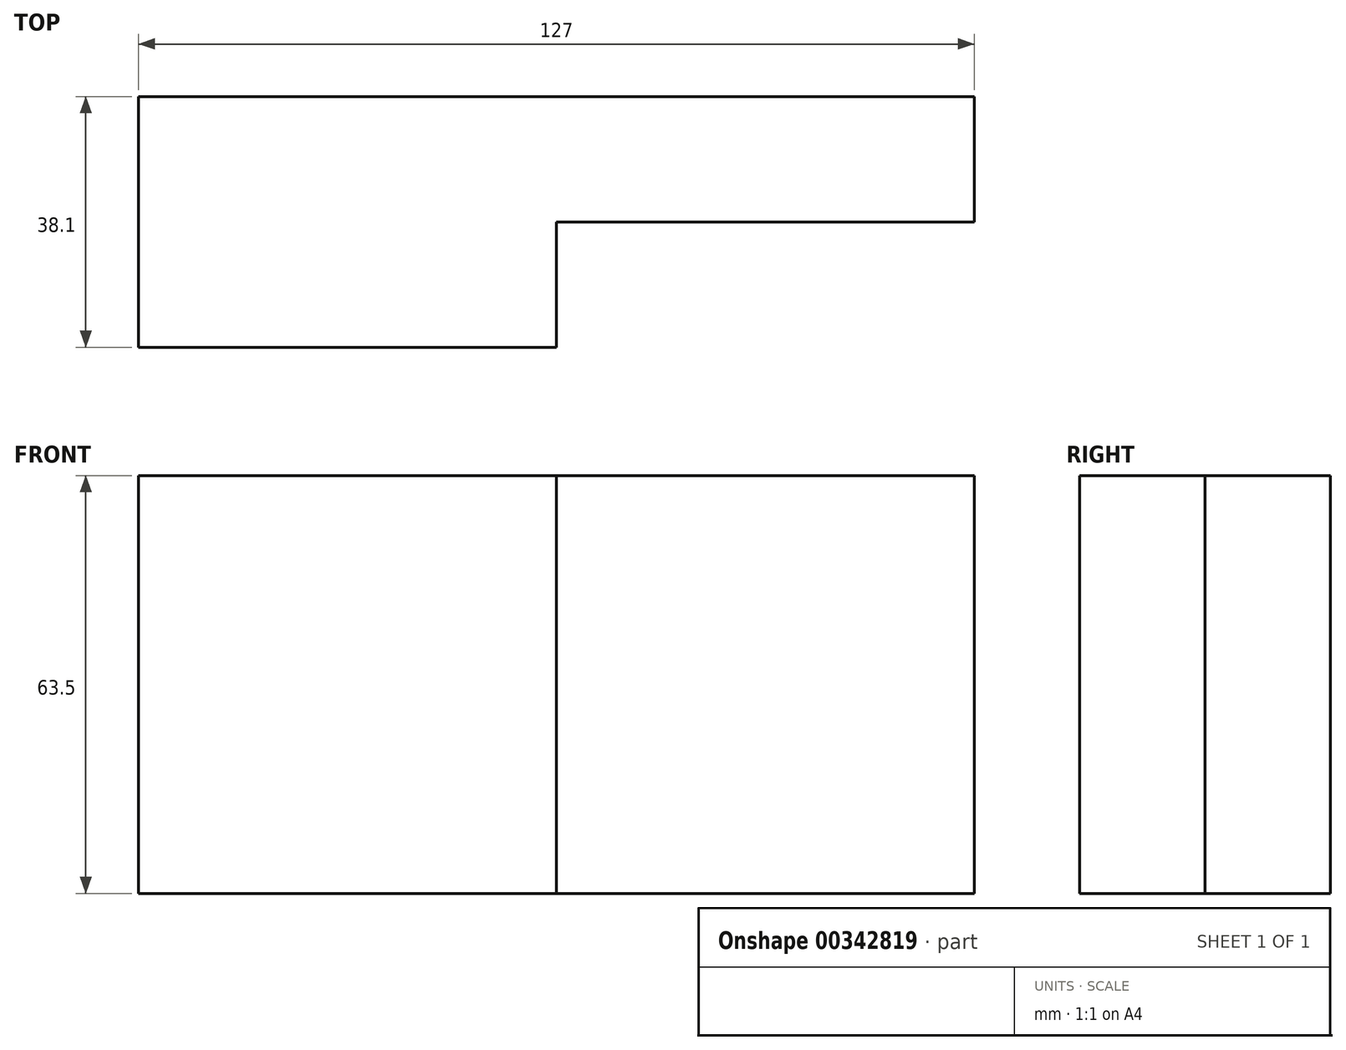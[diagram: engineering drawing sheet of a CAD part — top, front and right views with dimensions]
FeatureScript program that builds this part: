
annotation { "Feature Type Name" : "Feature", "Feature Type Description" : "" }
export const myFeature = defineFeature(function(context is Context, id is Id, definition is map)
    precondition{}
    {
        {
            var Q0;
            Q0=qCreatedBy(makeId("Top.planeOp"),FACE);
            var sketch = newSketch(context, id + "F0", { "sketchPlane" : qUnion([Q0])});
            skLineSegment(sketch, "E0", {"start": v(-47.05, 26.6) * mm, "end": v(-47.05, -11.5) * mm});
            skLineSegment(sketch, "E1", {"start": v(-47.05, 26.6) * mm, "end": v(79.95, 26.6) * mm});
            skLineSegment(sketch, "E2", {"start": v(79.95, 26.6) * mm, "end": v(79.95, 7.55) * mm});
            skLineSegment(sketch, "E3", {"start": v(79.95, 7.55) * mm, "end": v(16.45, 7.55) * mm});
            skLineSegment(sketch, "E4", {"start": v(-47.05, -11.5) * mm, "end": v(16.45, -11.5) * mm});
            skLineSegment(sketch, "E5", {"start": v(16.45, -11.5) * mm, "end": v(16.45, 7.55) * mm});
            skSolve(sketch);
        }
        {
            var Q0;
            Q0=makeQuery(id+"F0.imprint","IMPRINT",FACE,{"disambiguationData":[TD([[makeQuery(id+"F0.imprint","IMPRINT",EDGE,{"derivedFrom":sQuery(id+"F0.wireOp",EDGE,"E0")}),1.0]])]});
            extrude(context, id + "F1", {"entities" : qUnion([Q0]), "depth" : 63.5 * mm});
        }
    });
